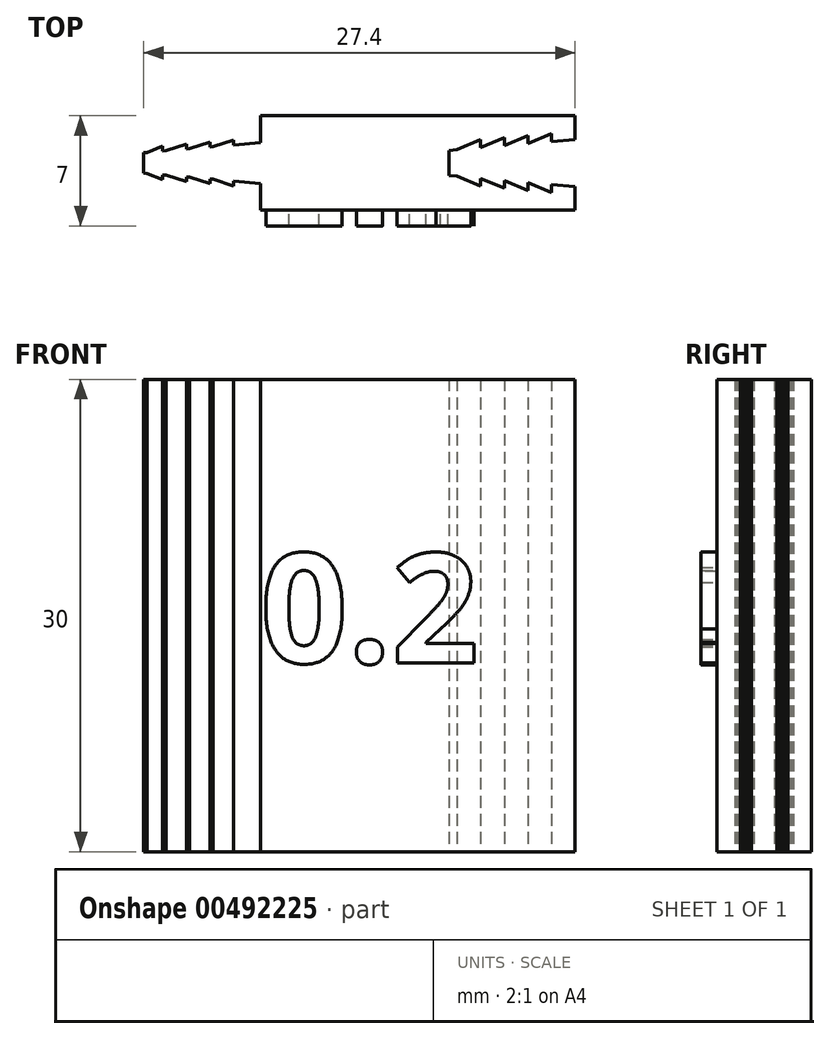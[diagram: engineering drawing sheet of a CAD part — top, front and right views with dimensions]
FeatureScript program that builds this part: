
annotation { "Feature Type Name" : "Feature", "Feature Type Description" : "" }
export const myFeature = defineFeature(function(context is Context, id is Id, definition is map)
    precondition{}
    {
        {
            var Q0;
            Q0=qCreatedBy(makeId("Top.planeOp"),FACE);
            var sketch = newSketch(context, id + "F0", { "sketchPlane" : qUnion([Q0])});
            skLineSegment(sketch, "E0", {"start": v(-19.4, 0) * mm, "end": v(11.33, 0) * mm, "construction": true});
            skLineSegment(sketch, "E1", {"start": v(0, 8.42) * mm, "end": v(0, -7.24) * mm, "construction": true});
            skLineSegment(sketch, "E2.bottom", {"start": v(10, -3) * mm, "end": v(-10, -3) * mm});
            skLineSegment(sketch, "E2.top", {"start": v(10, 3) * mm, "end": v(-10, 3) * mm});
            skLineSegment(sketch, "E2.left", {"start": v(10, -3) * mm, "end": v(10, -1.5) * mm});
            skLineSegment(sketch, "E2.right", {"start": v(-10, -3) * mm, "end": v(-10, 0) * mm});
            skPoint(sketch, "E2.middle", {"position": v(0, 0) * mm});
            skLineSegment(sketch, "E3", {"start": v(10, 1.5) * mm, "end": v(2, 0.8) * mm, "construction": true});
            skLineSegment(sketch, "E4", {"start": v(2, 0.8) * mm, "end": v(2, 0) * mm});
            skLineSegment(sketch, "E5", {"start": v(8.5, 1.37) * mm, "end": v(8.5, 1.87) * mm});
            skLineSegment(sketch, "E6", {"start": v(8.5, 1.87) * mm, "end": v(7, 1.24) * mm});
            skLineSegment(sketch, "E7", {"start": v(10, 1.5) * mm, "end": v(8.5, 1.37) * mm});
            skLineSegment(sketch, "E8", {"start": v(7, 1.24) * mm, "end": v(7, 1.74) * mm});
            skLineSegment(sketch, "E9", {"start": v(7, 1.74) * mm, "end": v(5.5, 1.1) * mm});
            skLineSegment(sketch, "E10", {"start": v(5.5, 1.1) * mm, "end": v(5.5, 1.6) * mm});
            skLineSegment(sketch, "E11", {"start": v(5.5, 1.6) * mm, "end": v(4, 0.98) * mm});
            skLineSegment(sketch, "E12", {"start": v(4, 0.98) * mm, "end": v(4, 1.48) * mm});
            skLineSegment(sketch, "E13", {"start": v(4, 1.48) * mm, "end": v(2.5, 0.84) * mm});
            skLineSegment(sketch, "E14", {"start": v(2, 0.8) * mm, "end": v(2.5, 0.84) * mm});
            skLineSegment(sketch, "E15.MirrorCS", {"start": v(2, -0.8) * mm, "end": v(2.5, -0.84) * mm});
            skLineSegment(sketch, "E16.MirrorCS", {"start": v(10, -1.5) * mm, "end": v(8.5, -1.37) * mm});
            skLineSegment(sketch, "E17.MirrorCS", {"start": v(10, -1.5) * mm, "end": v(2, -0.8) * mm, "construction": true});
            skLineSegment(sketch, "E18.MirrorCS", {"start": v(2, -0.8) * mm, "end": v(2, 0) * mm});
            skLineSegment(sketch, "E19.MirrorCS", {"start": v(8.5, -1.37) * mm, "end": v(8.5, -1.87) * mm});
            skLineSegment(sketch, "E20.MirrorCS", {"start": v(8.5, -1.87) * mm, "end": v(7, -1.24) * mm});
            skLineSegment(sketch, "E21.MirrorCS", {"start": v(4, -1.48) * mm, "end": v(2.5, -0.84) * mm});
            skLineSegment(sketch, "E22.MirrorCS", {"start": v(5.5, -1.1) * mm, "end": v(5.5, -1.6) * mm});
            skLineSegment(sketch, "E23.MirrorCS", {"start": v(7, -1.74) * mm, "end": v(5.5, -1.1) * mm});
            skLineSegment(sketch, "E24.MirrorCS", {"start": v(7, -1.24) * mm, "end": v(7, -1.74) * mm});
            skLineSegment(sketch, "E25.MirrorCS", {"start": v(4, -0.98) * mm, "end": v(4, -1.48) * mm});
            skLineSegment(sketch, "E26.MirrorCS", {"start": v(5.5, -1.6) * mm, "end": v(4, -0.98) * mm});
            skLineSegment(sketch, "E27.trimOffspring", {"start": v(10, 1.5) * mm, "end": v(10, 3) * mm});
            skLineSegment(sketch, "E28", {"start": v(-10, 1.3) * mm, "end": v(-17.4, 0.65) * mm, "construction": true});
            skLineSegment(sketch, "E29", {"start": v(-17.4, 0.65) * mm, "end": v(-17.4, 0) * mm});
            skLineSegment(sketch, "E30", {"start": v(-10, 1.3) * mm, "end": v(-11.7, 1.15) * mm});
            skLineSegment(sketch, "E31", {"start": v(-11.7, 1.15) * mm, "end": v(-11.7, 1.45) * mm});
            skLineSegment(sketch, "E32", {"start": v(-13.2, 1.02) * mm, "end": v(-13.2, 1.32) * mm});
            skLineSegment(sketch, "E33", {"start": v(-14.7, 0.89) * mm, "end": v(-14.7, 1.19) * mm});
            skLineSegment(sketch, "E34", {"start": v(-16.2, 0.76) * mm, "end": v(-16.2, 1.06) * mm});
            skLineSegment(sketch, "E35", {"start": v(-17.4, 0.65) * mm, "end": v(-17.2, 0.67) * mm});
            skLineSegment(sketch, "E36", {"start": v(-17.2, 0.67) * mm, "end": v(-16.2, 1.06) * mm});
            skLineSegment(sketch, "E37", {"start": v(-16.2, 0.76) * mm, "end": v(-16, 0.78) * mm});
            skLineSegment(sketch, "E38", {"start": v(-16, 0.78) * mm, "end": v(-14.7, 1.19) * mm});
            skLineSegment(sketch, "E39", {"start": v(-14.7, 0.89) * mm, "end": v(-14.5, 0.9) * mm});
            skLineSegment(sketch, "E40", {"start": v(-14.5, 0.9) * mm, "end": v(-13.2, 1.32) * mm});
            skLineSegment(sketch, "E41", {"start": v(-13.2, 1.02) * mm, "end": v(-13, 1.04) * mm});
            skLineSegment(sketch, "E42", {"start": v(-13, 1.04) * mm, "end": v(-11.7, 1.45) * mm});
            skLineSegment(sketch, "E43.trimOffspring", {"start": v(-10, 1.3) * mm, "end": v(-10, 3) * mm});
            skLineSegment(sketch, "E44.MirrorCS", {"start": v(-17.4, -0.65) * mm, "end": v(-17.2, -0.67) * mm});
            skLineSegment(sketch, "E45.MirrorCS", {"start": v(-14.7, -0.89) * mm, "end": v(-14.5, -0.9) * mm});
            skLineSegment(sketch, "E46.MirrorCS", {"start": v(-16.2, -0.76) * mm, "end": v(-16, -0.78) * mm});
            skLineSegment(sketch, "E47.MirrorCS", {"start": v(-13.2, -1.02) * mm, "end": v(-13, -1.04) * mm});
            skLineSegment(sketch, "E48.MirrorCS", {"start": v(-10, -1.3) * mm, "end": v(-11.7, -1.15) * mm});
            skLineSegment(sketch, "E49.MirrorCS", {"start": v(-11.7, -1.15) * mm, "end": v(-11.7, -1.45) * mm});
            skLineSegment(sketch, "E50.MirrorCS", {"start": v(-10, -1.3) * mm, "end": v(-17.4, -0.65) * mm, "construction": true});
            skLineSegment(sketch, "E51.MirrorCS", {"start": v(-17.2, -0.67) * mm, "end": v(-16.2, -1.06) * mm});
            skLineSegment(sketch, "E52.MirrorCS", {"start": v(-14.5, -0.9) * mm, "end": v(-13.2, -1.32) * mm});
            skLineSegment(sketch, "E53.MirrorCS", {"start": v(-16.2, -0.76) * mm, "end": v(-16.2, -1.06) * mm});
            skLineSegment(sketch, "E54.MirrorCS", {"start": v(-13.2, -1.02) * mm, "end": v(-13.2, -1.32) * mm});
            skLineSegment(sketch, "E55.MirrorCS", {"start": v(-17.4, -0.65) * mm, "end": v(-17.4, 0) * mm});
            skLineSegment(sketch, "E56.MirrorCS", {"start": v(-14.7, -0.89) * mm, "end": v(-14.7, -1.19) * mm});
            skLineSegment(sketch, "E57.MirrorCS", {"start": v(-13, -1.04) * mm, "end": v(-11.7, -1.45) * mm});
            skLineSegment(sketch, "E58.MirrorCS", {"start": v(-16, -0.78) * mm, "end": v(-14.7, -1.19) * mm});
            skSolve(sketch);
        }
        {
            var Q0;
            {var subQ0=sQuery(id+"F0.wireOp",EDGE,"E2.bottom");Q0=makeQuery(id+"F0.imprint","IMPRINT",FACE,{"disambiguationData":[TD([[makeQuery(id+"F0.imprint","IMPRINT",EDGE,{"derivedFrom":subQ0}),-1.0]])]});}
            extrude(context, id + "F1", {"entities" : qUnion([Q0]), "depth" : 30 * mm});
        }
        {
            var Q0;
            Q0=makeQuery(id+"F1.opExtrude","SWEPT_FACE",FACE,{"disambiguationData":[OSD([sQuery(id+"F0.wireOp",EDGE,"E2.bottom")])]});
            var sketch = newSketch(context, id + "F2", { "sketchPlane" : qUnion([Q0])});
            skText(sketch, "E59", { "text": "0.2", "fontName": "OpenSans-Bold.ttf"});
            const initialGuessF2  = {"E59": [-0.01, 0.012, 1, 0, 0.007]};
            skSetInitialGuess(sketch, initialGuessF2);
            skSolve(sketch);
        }
        {
            var Q0;
            Q0=makeQuery(id+"F2.imprint","IMPRINT",FACE,{"disambiguationData":[TD([[makeQuery(id+"F2.imprint","IMPRINT",EDGE,{"derivedFrom":sQuery(id+"F2.wireOp",EDGE,"E59.sketch_text.stroke-16")}),-1.0]])]});
            var Q1;
            Q1=makeQuery(id+"F2.imprint","IMPRINT",FACE,{"disambiguationData":[TD([[makeQuery(id+"F2.imprint","IMPRINT",EDGE,{"derivedFrom":sQuery(id+"F2.wireOp",EDGE,"E59.sketch_text.stroke-24")}),-1.0]])]});
            var Q2;
            Q2=makeQuery(id+"F2.imprint","IMPRINT",FACE,{"disambiguationData":[TD([[makeQuery(id+"F2.imprint","IMPRINT",EDGE,{"derivedFrom":sQuery(id+"F2.wireOp",EDGE,"E59.sketch_text.stroke-0")}),-1.0]])]});
            extrude(context, id + "F3", {"entities" : qUnion([Q0, Q1, Q2]), "operationType" : NewBodyOperationType.ADD, "depth" : 1 * mm});
        }
    });
